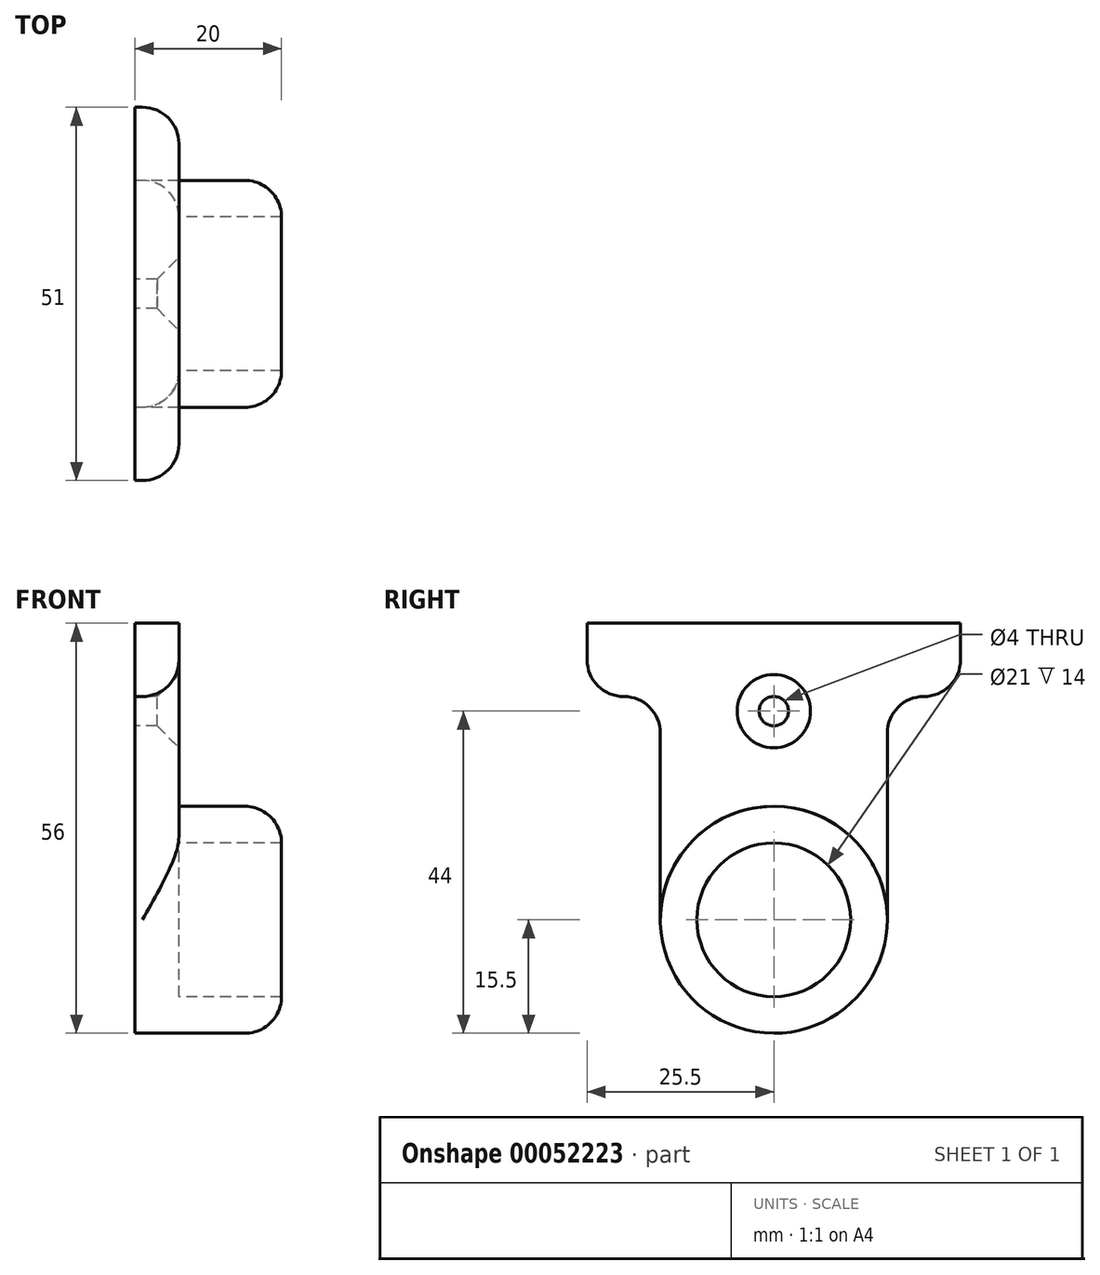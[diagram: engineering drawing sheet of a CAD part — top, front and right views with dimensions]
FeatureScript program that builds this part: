
annotation { "Feature Type Name" : "Feature", "Feature Type Description" : "" }
export const myFeature = defineFeature(function(context is Context, id is Id, definition is map)
    precondition{}
    {
        {
            var Q0;
            Q0=qCreatedBy(makeId("Right.planeOp"),FACE);
            var sketch = newSketch(context, id + "F0", { "sketchPlane" : qUnion([Q0])});
            skLineSegment(sketch, "E0.bottom", {"start": v(-15.5, 0) * mm, "end": v(15.5, 0) * mm});
            skLineSegment(sketch, "E0.top", {"start": v(-15.5, -40.5) * mm, "end": v(15.5, -40.5) * mm});
            skLineSegment(sketch, "E0.left", {"start": v(-15.5, 0) * mm, "end": v(-15.5, -40.5) * mm});
            skLineSegment(sketch, "E0.right", {"start": v(15.5, 0) * mm, "end": v(15.5, -40.5) * mm});
            skCircle(sketch, "E1", {"center": v(0, -40.5) * mm, "radius": 15.5 * mm});
            skCircle(sketch, "E2", {"center": v(0, -40.5) * mm, "radius": 10.5 * mm});
            skLineSegment(sketch, "E3.bottom", {"start": v(-25.5, 0) * mm, "end": v(25.5, 0) * mm});
            skLineSegment(sketch, "E3.top", {"start": v(-20.5, -10) * mm, "end": v(20.5, -10) * mm});
            skLineSegment(sketch, "E3.left", {"start": v(-25.5, 0) * mm, "end": v(-25.5, -5) * mm});
            skLineSegment(sketch, "E3.right", {"start": v(25.5, 0) * mm, "end": v(25.5, -5) * mm});
            skCircle(sketch, "E4", {"center": v(0, -12) * mm, "radius": 2 * mm});
            skPoint(sketch, "E5.visualSharp", {"position": v(-25.5, -10) * mm});
            skArc(sketch, "E5.filletArc", {"start": v(-25.5, -5) * mm, "mid": v(-24.04, -8.54) * mm, "end": v(-20.5, -10) * mm});
            skPoint(sketch, "E6.visualSharp", {"position": v(25.5, -10) * mm});
            skArc(sketch, "E6.filletArc", {"start": v(20.5, -10) * mm, "mid": v(24.04, -8.54) * mm, "end": v(25.5, -5) * mm});
            skLineSegment(sketch, "E7", {"start": v(0, 0) * mm, "end": v(0, -56) * mm, "construction": true});
            skSolve(sketch);
        }
        {
            var Q0;
            {var subQ4=sQuery(id+"F0.wireOp",EDGE,"E3.left");Q0=makeQuery(id+"F0.imprint","IMPRINT",FACE,{"disambiguationData":[TD([[makeQuery(id+"F0.imprint","IMPRINT",EDGE,{"derivedFrom":subQ4}),1.0]])]});}
            var Q1;
            {var subQ1=sQuery(id+"F0.wireOp",EDGE,"E0.left");var subQ4=sQuery(id+"F0.wireOp",EDGE,"E3.bottom");var subQ5=makeQuery(id+"F0.imprint","INTERSECT",VERTEX,{"derivedFrom":[subQ1,subQ4]});Q1=makeQuery(id+"F0.imprint","IMPRINT",FACE,{"disambiguationData":[TD([[makeQuery(id+"F0.imprint","IMPRINT",EDGE,{"disambiguationData":[TD([[subQ5,-1.0]])],"derivedFrom":subQ1}),1.0]])]});}
            var Q2;
            {var subQ6=sQuery(id+"F0.wireOp",EDGE,"E3.right");Q2=makeQuery(id+"F0.imprint","IMPRINT",FACE,{"disambiguationData":[TD([[makeQuery(id+"F0.imprint","IMPRINT",EDGE,{"derivedFrom":subQ6}),-1.0]])]});}
            var Q3;
            {var subQ3=sQuery(id+"F0.wireOp",EDGE,"E4");Q3=makeQuery(id+"F0.imprint","IMPRINT",FACE,{"disambiguationData":[TD([[makeQuery(id+"F0.imprint","IMPRINT",EDGE,{"derivedFrom":subQ3}),-1.0]])]});}
            var Q4;
            {var subQ1=sQuery(id+"F0.wireOp",EDGE,"E0.top");var subQ3=sQuery(id+"F0.wireOp",EDGE,"E2");var subQ4=makeQuery(id+"F0.imprint","INTERSECT",VERTEX,{"disambiguationData":[OD(0.0)],"derivedFrom":[subQ1,subQ3]});Q4=makeQuery(id+"F0.imprint","IMPRINT",FACE,{"disambiguationData":[TD([[makeQuery(id+"F0.imprint","IMPRINT",EDGE,{"disambiguationData":[TD([[subQ4,1.0]])],"derivedFrom":subQ3}),-1.0]])]});}
            var Q5;
            {var subQ1=sQuery(id+"F0.wireOp",EDGE,"E0.top");var subQ3=sQuery(id+"F0.wireOp",EDGE,"E2");var subQ4=makeQuery(id+"F0.imprint","INTERSECT",VERTEX,{"disambiguationData":[OD(0.0)],"derivedFrom":[subQ1,subQ3]});Q5=makeQuery(id+"F0.imprint","IMPRINT",FACE,{"disambiguationData":[TD([[makeQuery(id+"F0.imprint","IMPRINT",EDGE,{"disambiguationData":[TD([[subQ4,-1.0]])],"derivedFrom":subQ3}),-1.0]])]});}
            var Q6;
            {var subQ0=sQuery(id+"F0.wireOp",EDGE,"E2");var subQ1=sQuery(id+"F0.wireOp",EDGE,"E0.top");var subQ2=makeQuery(id+"F0.imprint","INTERSECT",VERTEX,{"disambiguationData":[OD(0.0)],"derivedFrom":[subQ1,subQ0]});Q6=makeQuery(id+"F0.imprint","IMPRINT",FACE,{"disambiguationData":[TD([[makeQuery(id+"F0.imprint","IMPRINT",EDGE,{"disambiguationData":[TD([[subQ2,-1.0]])],"derivedFrom":subQ1}),-1.0]])]});}
            var Q7;
            {var subQ0=sQuery(id+"F0.wireOp",EDGE,"E2");var subQ1=sQuery(id+"F0.wireOp",EDGE,"E0.top");var subQ2=makeQuery(id+"F0.imprint","INTERSECT",VERTEX,{"disambiguationData":[OD(0.0)],"derivedFrom":[subQ1,subQ0]});Q7=makeQuery(id+"F0.imprint","IMPRINT",FACE,{"disambiguationData":[TD([[makeQuery(id+"F0.imprint","IMPRINT",EDGE,{"disambiguationData":[TD([[subQ2,-1.0]])],"derivedFrom":subQ1}),1.0]])]});}
            extrude(context, id + "F1", {"entities" : qUnion([Q0, Q1, Q2, Q3, Q4, Q5, Q6, Q7]), "depth" : 6 * mm});
        }
        {
            var Q0;
            {var subQ1=sQuery(id+"F0.wireOp",EDGE,"E0.top");var subQ3=sQuery(id+"F0.wireOp",EDGE,"E2");var subQ4=makeQuery(id+"F0.imprint","INTERSECT",VERTEX,{"disambiguationData":[OD(0.0)],"derivedFrom":[subQ1,subQ3]});Q0=makeQuery(id+"F0.imprint","IMPRINT",FACE,{"disambiguationData":[TD([[makeQuery(id+"F0.imprint","IMPRINT",EDGE,{"disambiguationData":[TD([[subQ4,-1.0]])],"derivedFrom":subQ3}),-1.0]])]});}
            var Q1;
            {var subQ1=sQuery(id+"F0.wireOp",EDGE,"E0.top");var subQ3=sQuery(id+"F0.wireOp",EDGE,"E2");var subQ4=makeQuery(id+"F0.imprint","INTERSECT",VERTEX,{"disambiguationData":[OD(0.0)],"derivedFrom":[subQ1,subQ3]});Q1=makeQuery(id+"F0.imprint","IMPRINT",FACE,{"disambiguationData":[TD([[makeQuery(id+"F0.imprint","IMPRINT",EDGE,{"disambiguationData":[TD([[subQ4,1.0]])],"derivedFrom":subQ3}),-1.0]])]});}
            extrude(context, id + "F2", {"entities" : qUnion([Q0, Q1]), "operationType" : NewBodyOperationType.ADD, "depth" : 20 * mm});
        }
        {
            var Q0;
            Q0=makeQuery(id+"F1.opExtrude","CAP_EDGE",EDGE,{"disambiguationData":[OSD([sQuery(id+"F0.wireOp",EDGE,"E4")])],"isStart":false});
            chamfer(context, id + "F3", {"entities" : qUnion([Q0]), "width" : 3 * mm, "tangentPropagation" : true});
        }
        {
            var Q0;
            Q0=makeQuery(id+"F1.opExtrude","SWEPT_EDGE",EDGE,{"disambiguationData":[OSD([sQuery(id+"F0.wireOp",EDGE,"E0.right"),sQuery(id+"F0.wireOp",EDGE,"E3.top")])]});
            var Q1;
            Q1=makeQuery(id+"F1.opExtrude","SWEPT_EDGE",EDGE,{"disambiguationData":[OSD([sQuery(id+"F0.wireOp",EDGE,"E0.left"),sQuery(id+"F0.wireOp",EDGE,"E3.top")])]});
            fillet(context, id + "F4", {"entities" : qUnion([Q0, Q1]), "radius" : 5 * mm, "tangentPropagation" : true, "allowEdgeOverflow" : false});
        }
        {
            var Q0;
            Q0=makeQuery(id+"F1.opExtrude","CAP_EDGE",EDGE,{"disambiguationData":[OSD([sQuery(id+"F0.wireOp",EDGE,"E5.filletArc")])],"isStart":false});
            var Q1;
            Q1=makeQuery(id+"F1.opExtrude","CAP_EDGE",EDGE,{"disambiguationData":[OSD([sQuery(id+"F0.wireOp",EDGE,"E0.right")])],"isStart":false});
            var Q2;
            Q2=makeQuery(id+"F2.opExtrude","CAP_EDGE",EDGE,{"disambiguationData":[OSD([sQuery(id+"F0.wireOp",EDGE,"E1")])],"isStart":false});
            fillet(context, id + "F5", {"entities" : qUnion([Q0, Q1, Q2]), "radius" : 5 * mm, "tangentPropagation" : true, "allowEdgeOverflow" : false});
        }
    });
